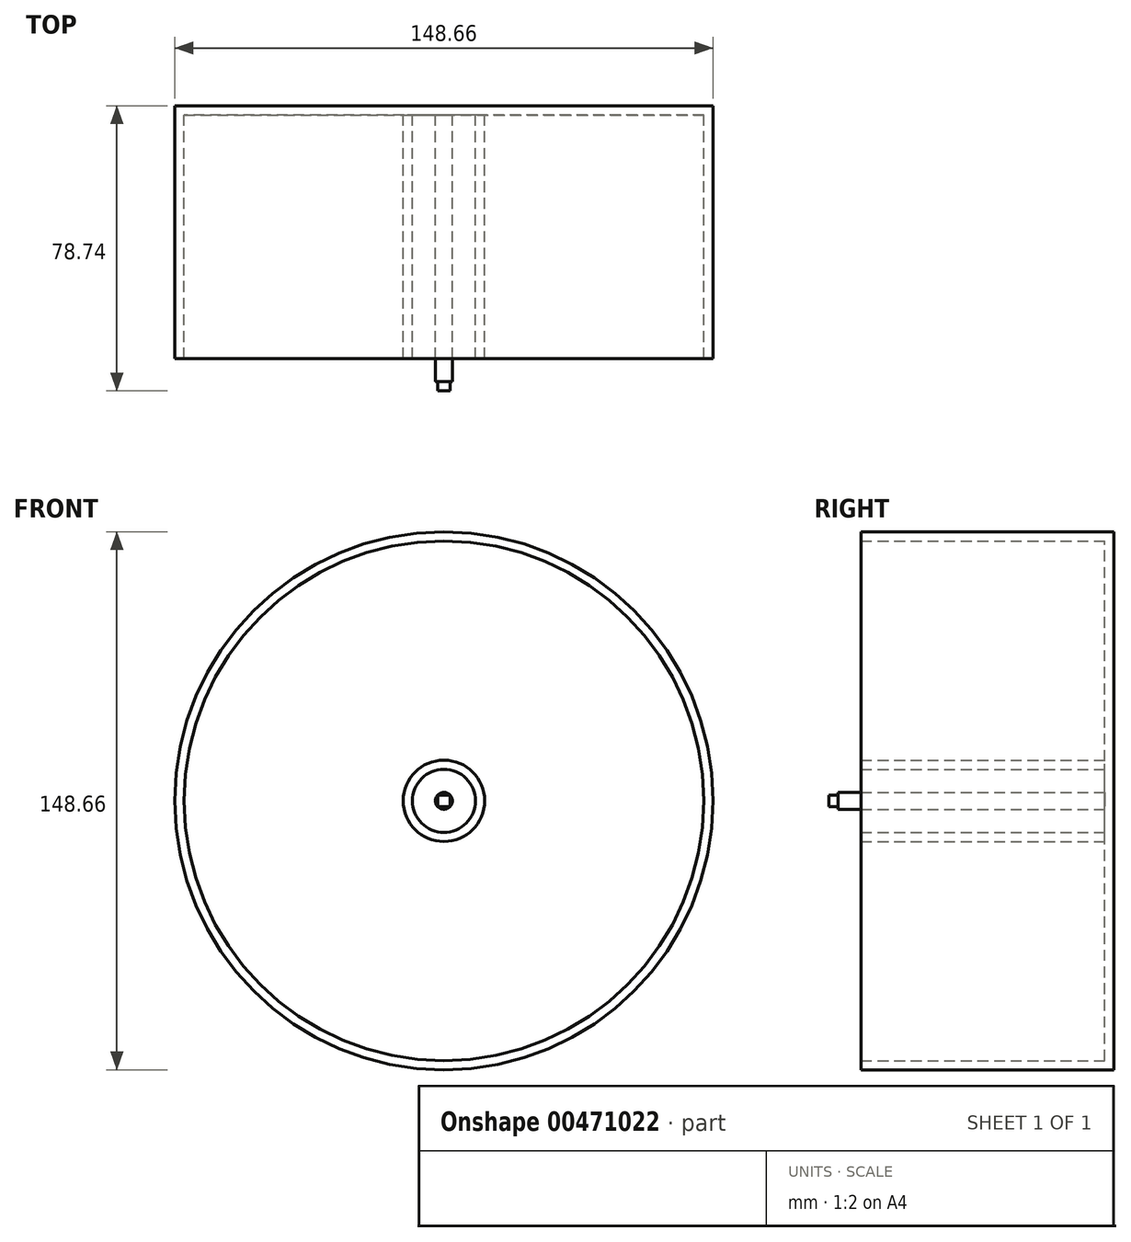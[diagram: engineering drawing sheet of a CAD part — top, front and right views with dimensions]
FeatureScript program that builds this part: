
annotation { "Feature Type Name" : "Feature", "Feature Type Description" : "" }
export const myFeature = defineFeature(function(context is Context, id is Id, definition is map)
    precondition{}
    {
        {
            var Q0;
            Q0=qCreatedBy(makeId("Front.planeOp"),FACE);
            var sketch = newSketch(context, id + "F0", { "sketchPlane" : qUnion([Q0])});
            skCircle(sketch, "E0", {"center": v(0, 0) * mm, "radius": 74.33 * mm});
            skSolve(sketch);
        }
        {
            var Q0;
            Q0=makeQuery(id+"F0.imprint","IMPRINT",FACE,{"disambiguationData":[TD([[makeQuery(id+"F0.imprint","IMPRINT",EDGE,{"derivedFrom":sQuery(id+"F0.wireOp",EDGE,"E0")}),1.0]])]});
            extrude(context, id + "F1", {"entities" : qUnion([Q0]), "depth" : 69.85 * mm});
        }
        {
            var Q0;
            Q0=makeQuery(id+"F1.opExtrude","CAP_FACE",FACE,{"disambiguationData":[OSD([sQuery(id+"F0.wireOp",EDGE,"E0")])],"isStart":false});
            shell(context, id + "F2", {"entities" : qUnion([Q0]), "thickness" : 2.54 * mm});
        }
        {
            var Q0;
            {var subQ0=sQuery(id+"F0.wireOp",EDGE,"E0");Q0=makeQuery(id+"F2.opShell","OFFSET_FACE",FACE,{"disambiguationData":[OSD([subQ0]),TDD([makeQuery(id+"F1.opExtrude","CAP_FACE",FACE,{"disambiguationData":[OSD([subQ0])],"isStart":true})])]});}
            var sketch = newSketch(context, id + "F3", { "sketchPlane" : qUnion([Q0])});
            skCircle(sketch, "E1", {"center": v(0, 0) * mm, "radius": 11.25 * mm});
            skSolve(sketch);
        }
        {
            var Q0;
            Q0=makeQuery(id+"F3.imprint","IMPRINT",FACE,{"disambiguationData":[TD([[makeQuery(id+"F3.imprint","IMPRINT",EDGE,{"derivedFrom":sQuery(id+"F3.wireOp",EDGE,"E1")}),1.0]])]});
            extrude(context, id + "F4", {"entities" : qUnion([Q0]), "operationType" : NewBodyOperationType.ADD, "depth" : 67.3 * mm});
        }
        {
            var Q0;
            Q0=makeQuery(id+"F4.opExtrude","CAP_FACE",FACE,{"disambiguationData":[OSD([sQuery(id+"F3.wireOp",EDGE,"E1")])],"isStart":false});
            shell(context, id + "F5", {"entities" : qUnion([Q0]), "thickness" : 2.54 * mm});
        }
        {
            var Q0;
            Q0=makeQuery(id+"F5.opShell","OFFSET_FACE",FACE,{"disambiguationData":[OSD([sQuery(id+"F0.wireOp",EDGE,"E0")])]});
            var sketch = newSketch(context, id + "F6", { "sketchPlane" : qUnion([Q0])});
            skCircle(sketch, "E2", {"center": v(0, 0) * mm, "radius": 2.33 * mm});
            skSolve(sketch);
        }
        {
            var Q0;
            Q0=makeQuery(id+"F6.imprint","IMPRINT",FACE,{"disambiguationData":[TD([[makeQuery(id+"F6.imprint","IMPRINT",EDGE,{"derivedFrom":sQuery(id+"F6.wireOp",EDGE,"E2")}),1.0]])]});
            extrude(context, id + "F7", {"entities" : qUnion([Q0]), "operationType" : NewBodyOperationType.ADD, "depth" : 73.66 * mm});
        }
        {
            var Q0;
            Q0=makeQuery(id+"F7.opExtrude","CAP_FACE",FACE,{"disambiguationData":[OSD([sQuery(id+"F6.wireOp",EDGE,"E2")])],"isStart":false});
            var sketch = newSketch(context, id + "F8", { "sketchPlane" : qUnion([Q0])});
            skLineSegment(sketch, "E3.bottom", {"start": v(-1.73, 1.55) * mm, "end": v(1.67, 1.55) * mm});
            skLineSegment(sketch, "E3.top", {"start": v(-1.73, -1.62) * mm, "end": v(1.67, -1.62) * mm});
            skLineSegment(sketch, "E3.left", {"start": v(-1.73, 1.55) * mm, "end": v(-1.73, -1.62) * mm});
            skLineSegment(sketch, "E3.right", {"start": v(1.67, 1.55) * mm, "end": v(1.67, -1.62) * mm});
            skSolve(sketch);
        }
        {
            var Q0;
            {var subQ1=sQuery(id+"F8.wireOp",EDGE,"E3.bottom");Q0=makeQuery(id+"F8.imprint","IMPRINT",FACE,{"disambiguationData":[TD([[makeQuery(id+"F8.imprint","IMPRINT",EDGE,{"derivedFrom":subQ1}),-1.0]])]});}
            extrude(context, id + "F9", {"entities" : qUnion([Q0]), "operationType" : NewBodyOperationType.ADD, "depth" : 2.54 * mm});
        }
    });
